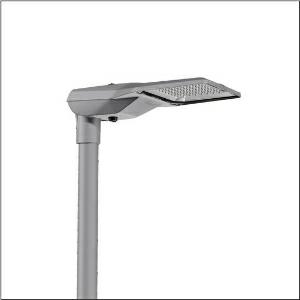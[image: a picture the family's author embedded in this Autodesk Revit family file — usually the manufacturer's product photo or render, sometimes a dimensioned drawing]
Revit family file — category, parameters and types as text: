
# Revit family: streetlight_sl_21_midi___stw1_0a_5xe3e33t08nb_95e0
name_source: partatom
category: Lighting Fixtures
units: mm (PartAtom-declared; Revit-internal decimal feet)

## family parameters
Cut with Voids When Loaded = No
Host = Face
Light Source = No
Part Type = Normal
Room Calculation Point = No
Round Connector Dimension = Use Diameter
Shared = No

## types (1)
- --- (1 x LED, 22700 lm, 151.2 W, 3000K)
    Apparent Load = 151 VA
    CIE Flux Codes = 39 75 98 100 100
    Color Rendering = 70
    Color Temperature = 3000K
    Default Elevation = 1800 mm
    Description = Streetlight SL 21 midi, mast luminaire, primary light control with lens, of PMMA, primary optical cover: cover, of toughened safety glass, transparent, light distribution: STW1.0a, light emission: direct distribution, primary light characteristic: asymmetric, installation type: side-entry, post-top, LED, High Power LED, rated luminous flux: 22.700lm, luminous efficacy: 150lm/W, light colour: 730, colour temperature: 3000K, control gear: D4i, control: overheat protection, constant luminous flux control, time-dependent luminous flux control, flexible luminous flux parameterisation, pre-setting: logarithmic dimming characteristic, mains connection: 230..240V, AC, 50/60Hz, start of lifetime: 151W, end of service life: 157W, reduction: 70W, luminaire housing, of diecast aluminium, powder-coated, SITECO metallic grey (DB 702S), corrosivity category C5 high according to DIN EN ISO 12944, please order mast flange separately, inclination adjustable: 0°, 5°, 10°, 15°, sealing non-destructively replaceable, multi-level sealing system, length: 644mm, width: 335mm, height: 110mm, mast flange for spigot size: 42mm (side-entry): 5XC10008XM4, 60/48mm (side-entry/post-top): 5XC10108XM2, 76/60mm (side-entry/post-top): 5XC10108XM1, mounting height: 4..8m, Smart Interface below and above, protection rating (complete): IP66, insulation class (complete): insulation class II (safety insulation), certification: CE, ENEC, ENEC+, VDE, impact resistance: IK10, permissible operating ambient temperature for outdoor applications: -40..+50°C, standard-compliant lighting for roads and squares, packaging unit: 1 piece

Light Distribution: STW1.0a
    Height = 111 mm
    Lamp = 1 x LED
    Lamp Light Flux = 22700 lm
    Lamp Power = 151.2 W
    Lamp count = 1
    Length = 644 mm
    Luminous efficacy = 150 lm/W
    Manufacturer = Siteco
    ModVariant = No
    Model = 5XE3E33T08NB
    Number of Poles = 1
    OnlyDefault = Yes
    Power Factor = 1
    Product Name = Streetlight SL 21 midi | STW1.0a
    Product group = mast luminaire | pylon top
    ProductGroupID = 6100
    Protection Class = Protection class II
    Protection Degree = IP 66
    RLX_Detail_Level = 1
    RLX_Emergency_Light_Flux = 0 lm
    RLX_Emergency_Type = 0
    RLX_Emergency_Type_DB = No
    RlxData = <blob elided: 27093 chars, md5=28802af2>
    Socket = socket
    Standby Power = 0 W
    System Light Flux = 22700 lm
    System Power = 151 W
    Type Comments = factory setting: luminous flux: 100 % | dim-lin: 254 | 802 mA
    Type Image = l_1004304.jpg
    URL = http://relux.com
    VarID = @adj_169049
    Voltage = 0 V
    Weight = 0.00 kg
    Width = 336 mm

## geometry (parser evidence)
native form markers: Blend x4, Sweep x11
no freeform markers — native parametric forms only
